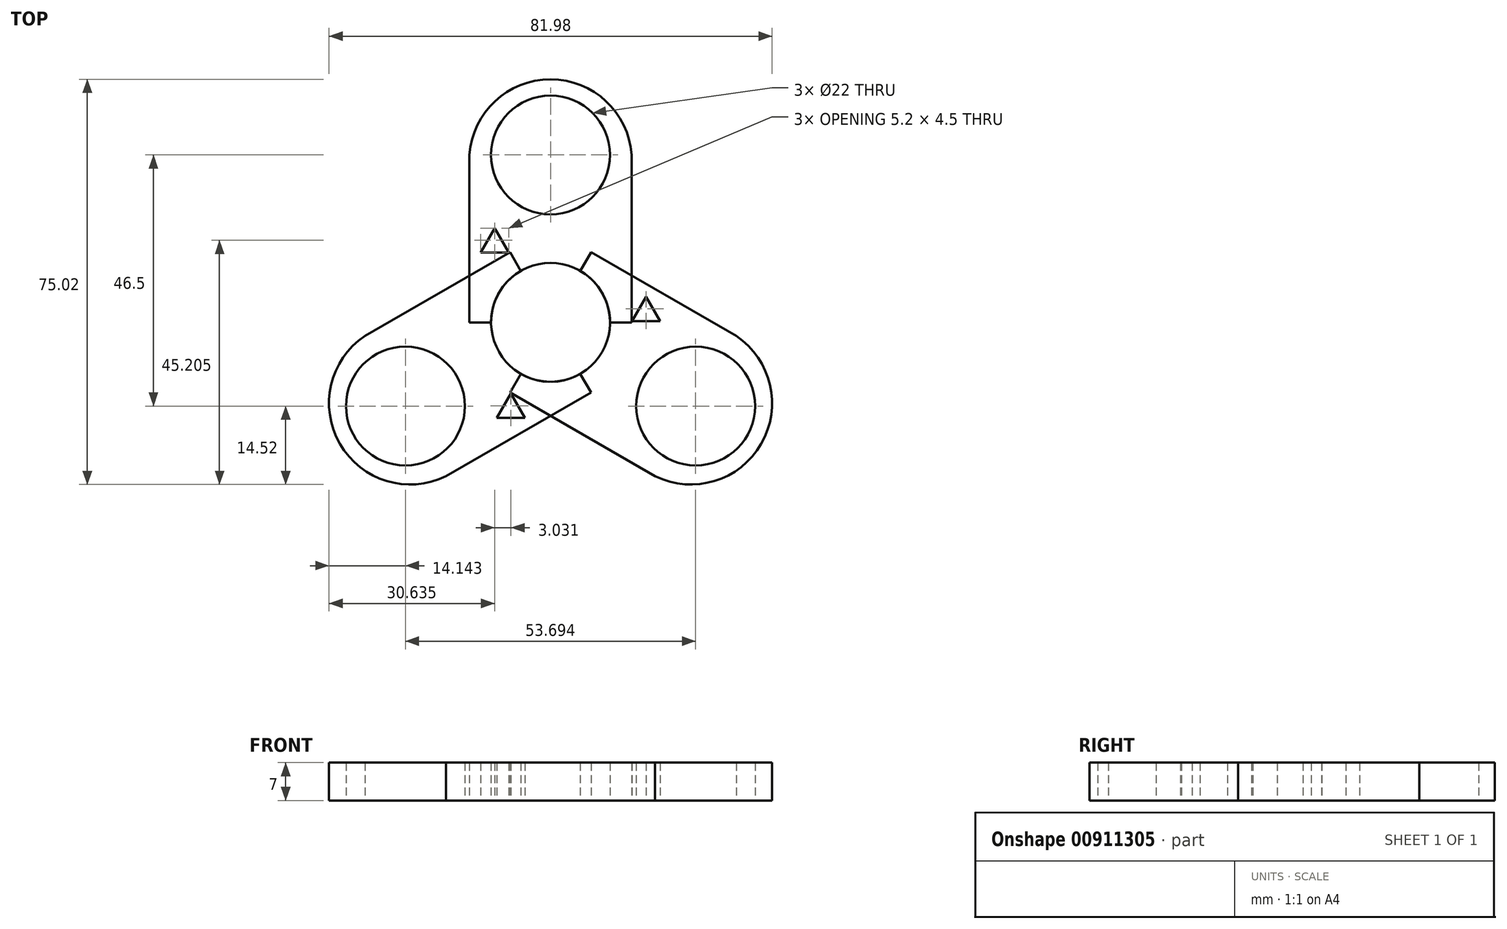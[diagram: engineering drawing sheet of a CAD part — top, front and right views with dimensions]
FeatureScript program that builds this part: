
annotation { "Feature Type Name" : "Feature", "Feature Type Description" : "" }
export const myFeature = defineFeature(function(context is Context, id is Id, definition is map)
    precondition{}
    {
        {
            var Q0;
            Q0=qCreatedBy(makeId("Top.planeOp"),FACE);
            var sketch = newSketch(context, id + "F0", { "sketchPlane" : qUnion([Q0])});
            skCircle(sketch, "E0", {"center": v(0, 0) * mm, "radius": 11 * mm});
            skLineSegment(sketch, "E1", {"start": v(0, 0) * mm, "end": v(0, 45) * mm});
            skLineSegment(sketch, "E2", {"start": v(0, 45) * mm, "end": v(15, 45) * mm});
            skLineSegment(sketch, "E3", {"start": v(15, 45) * mm, "end": v(15, 0) * mm});
            skLineSegment(sketch, "E4", {"start": v(15, 0) * mm, "end": v(0, 0) * mm});
            skLineSegment(sketch, "E5", {"start": v(0, 0) * mm, "end": v(-15, 0) * mm});
            skLineSegment(sketch, "E6", {"start": v(-15, 0) * mm, "end": v(-15, 45) * mm});
            skLineSegment(sketch, "E7", {"start": v(-15, 45) * mm, "end": v(0, 45) * mm});
            skLineSegment(sketch, "E8", {"start": v(0, 45) * mm, "end": v(0, 31) * mm});
            skCircle(sketch, "E9", {"center": v(0, 31) * mm, "radius": 11 * mm});
            skArc(sketch, "E10", {"start": v(15, 31) * mm, "mid": v(10.26, 40.96) * mm, "end": v(0, 45) * mm});
            skArc(sketch, "E11", {"start": v(0, 45) * mm, "mid": v(-10.26, 40.96) * mm, "end": v(-15, 31) * mm});
            skCircle(sketch, "E12.cCircle", {"center": v(-10.35, 14.44) * mm, "radius": 1.5 * mm, "construction": true});
            skLineSegment(sketch, "E12.0", {"start": v(-7.76, 12.94) * mm, "end": v(-12.95, 12.94) * mm});
            skLineSegment(sketch, "E12.1", {"start": v(-12.95, 12.94) * mm, "end": v(-10.35, 17.44) * mm});
            skLineSegment(sketch, "E12.2", {"start": v(-10.35, 17.44) * mm, "end": v(-7.76, 12.94) * mm});
            skPoint(sketch, "E12.0.midPoint", {"position": v(-10.35, 12.94) * mm});
            skPoint(sketch, "E13.cCircle.centerSnap0", {"position": v(-9.06, 15.19) * mm});
            skSolve(sketch);
        }
        {
            var Q0;
            Q0=qCreatedBy(makeId("Front.planeOp"),FACE);
            var sketch = newSketch(context, id + "F1", { "sketchPlane" : qUnion([Q0])});
            skLineSegment(sketch, "E14", {"start": v(0, 0) * mm, "end": v(0, 39.05) * mm});
            skLineSegment(sketch, "E15", {"start": v(0, 39.05) * mm, "end": v(0, 0) * mm});
            skSolve(sketch);
        }
        {
            var Q0;
            {var subQ3=sQuery(id+"F0.wireOp",EDGE,"E10");Q0=makeQuery(id+"F0.imprint","IMPRINT",FACE,{"disambiguationData":[TD([[makeQuery(id+"F0.imprint","IMPRINT",EDGE,{"derivedFrom":subQ3}),1.0]])]});}
            var Q1;
            {var subQ3=sQuery(id+"F0.wireOp",EDGE,"E11");Q1=makeQuery(id+"F0.imprint","IMPRINT",FACE,{"disambiguationData":[TD([[makeQuery(id+"F0.imprint","IMPRINT",EDGE,{"derivedFrom":subQ3}),1.0]])]});}
            extrude(context, id + "F2", {"entities" : qUnion([Q0, Q1]), "depth" : 7 * mm, "offsetDistance" : 25 * mm});
        }
        {
            var Q0;
            Q0=makeQuery(id+"F2.opExtrude","SWEPT_BODY",BODY,{"disambiguationData":[OSD([sQuery(id+"F0.wireOp",EDGE,"E0"),sQuery(id+"F0.wireOp",EDGE,"E3"),sQuery(id+"F0.wireOp",EDGE,"E4"),sQuery(id+"F0.wireOp",EDGE,"E5"),sQuery(id+"F0.wireOp",EDGE,"E6"),sQuery(id+"F0.wireOp",EDGE,"E9"),sQuery(id+"F0.wireOp",EDGE,"E10"),sQuery(id+"F0.wireOp",EDGE,"E11")])]});
            var Q1;
            Q1=sQuery(id+"F1.wireOp",EDGE,"E15");
            transform(context, id + "F3", {"entities" : qUnion([Q0]), "transformType" : TransformType.ROTATION, "transformAxis" : qUnion([Q1]), "angle" : 120 * degree, "makeCopy" : true});
        }
        {
            var Q0;
            Q0=makeQuery(id+"F3.opPattern","COPY",BODY,{"derivedFrom":makeQuery(id+"F2.opExtrude","SWEPT_BODY",BODY,{"disambiguationData":[OSD([sQuery(id+"F0.wireOp",EDGE,"E0"),sQuery(id+"F0.wireOp",EDGE,"E3"),sQuery(id+"F0.wireOp",EDGE,"E4"),sQuery(id+"F0.wireOp",EDGE,"E5"),sQuery(id+"F0.wireOp",EDGE,"E6"),sQuery(id+"F0.wireOp",EDGE,"E9"),sQuery(id+"F0.wireOp",EDGE,"E10"),sQuery(id+"F0.wireOp",EDGE,"E11")])]}),"instanceName":"1"});
            var Q1;
            Q1=sQuery(id+"F1.wireOp",EDGE,"E15");
            transform(context, id + "F4", {"entities" : qUnion([Q0]), "transformType" : TransformType.ROTATION, "transformAxis" : qUnion([Q1]), "angle" : 120 * degree, "makeCopy" : true});
        }
    });
